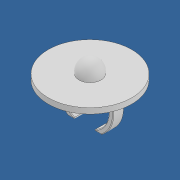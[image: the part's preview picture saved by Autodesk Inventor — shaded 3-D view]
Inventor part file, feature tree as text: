
AUTODESK INVENTOR PART (.ipt)
format: ipt  version: 2022.5 (Build 265521000, 521)  size: 193,536 bytes
history: native  units: mm
features: other x2, fillet x2, sketch x2, extrude x1
ambient origin geometry x8: Origin, YZ Plane, XZ Plane, XY Plane, X Axis, Y Axis, Z Axis, Center Point
bodies: Body1 (feature_tree)
feature tree (7):
  other  "實體1"
  other  "迴轉1"
  extrude  "擠出1"  Depth=38.0mm
  fillet  "圓角1"  Radius=3.488mm
  fillet  "圓角2"  [1 undecoded]
  sketch  "草圖1"
  sketch  "草圖2"
note: 1 required parameter value undecoded (feature->parameter linkage not recoverable at this tier; creation-order binding heuristic only, values carry confidence <= 0.55)
